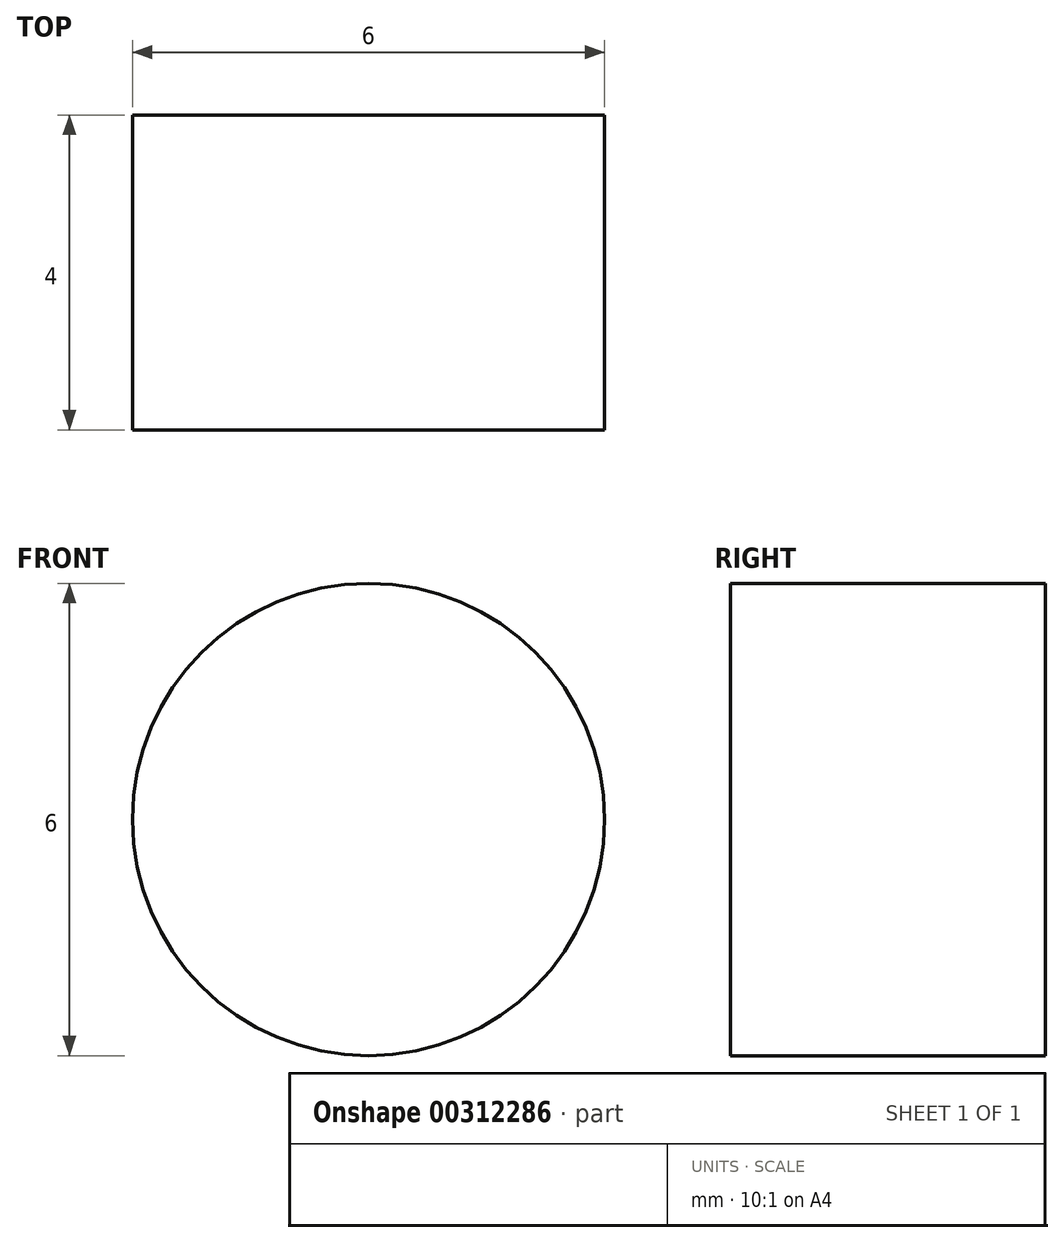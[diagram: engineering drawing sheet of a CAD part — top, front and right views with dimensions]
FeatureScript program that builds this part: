
annotation { "Feature Type Name" : "Feature", "Feature Type Description" : "" }
export const myFeature = defineFeature(function(context is Context, id is Id, definition is map)
    precondition{}
    {
        {
            var Q0;
            Q0=qCreatedBy(makeId("Front.planeOp"),FACE);
            var sketch = newSketch(context, id + "F0", { "sketchPlane" : qUnion([Q0])});
            skCircle(sketch, "E0", {"center": v(0, 0) * mm, "radius": 3 * mm});
            skSolve(sketch);
        }
        {
            var Q0;
            Q0=qSketchRegion(id+"F0",true);
            extrude(context, id + "F1", {"entities" : qUnion([Q0]), "depth" : 4 * mm});
        }
    });
